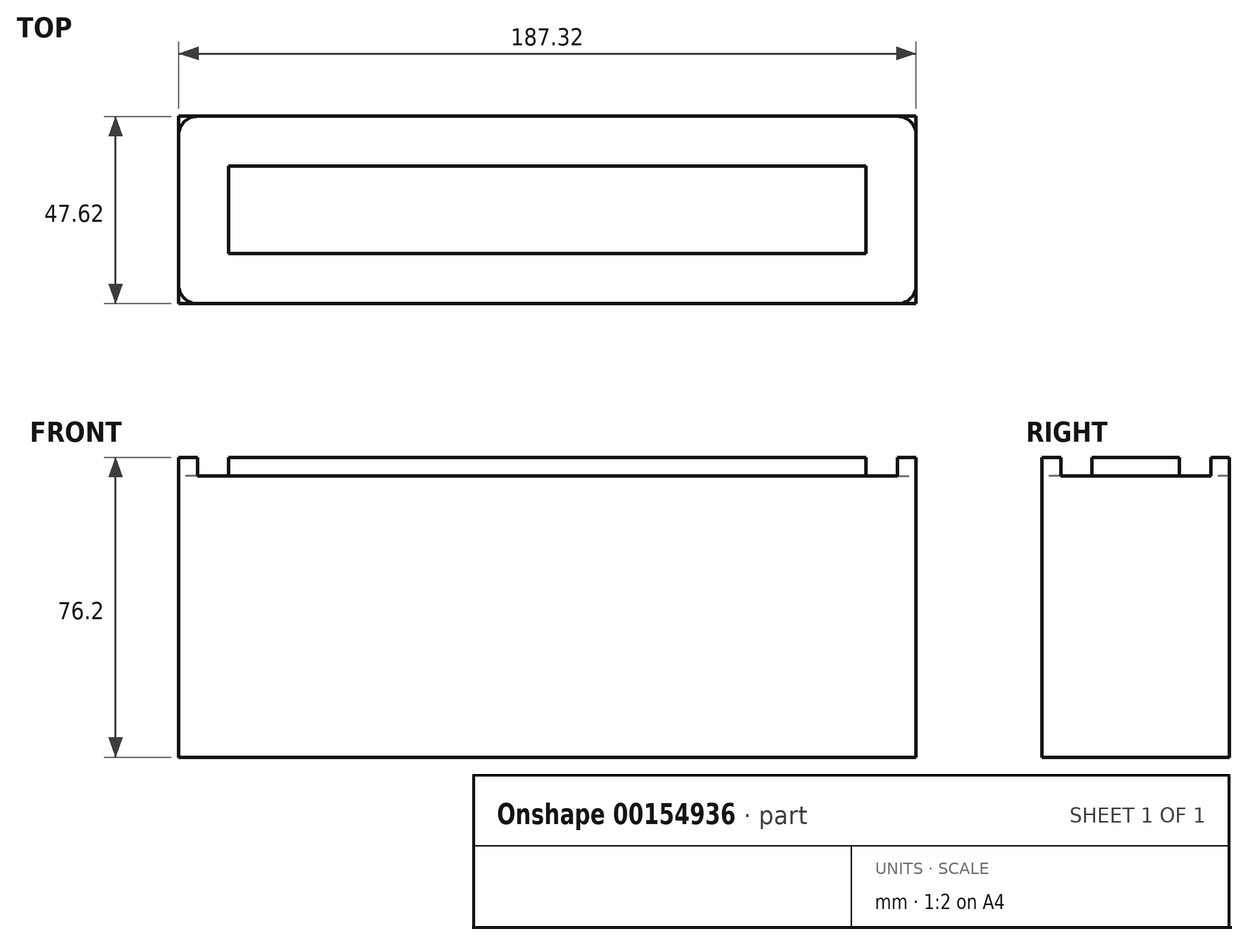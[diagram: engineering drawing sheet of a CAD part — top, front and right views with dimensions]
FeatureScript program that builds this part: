
annotation { "Feature Type Name" : "Feature", "Feature Type Description" : "" }
export const myFeature = defineFeature(function(context is Context, id is Id, definition is map)
    precondition{}
    {
        {
            var Q0;
            Q0=qCreatedBy(makeId("Top.planeOp"),FACE);
            var sketch = newSketch(context, id + "F0", { "sketchPlane" : qUnion([Q0])});
            skLineSegment(sketch, "E0.bottom", {"start": v(4.76, 0) * mm, "end": v(182.56, 0) * mm});
            skLineSegment(sketch, "E0.top", {"start": v(4.76, 47.63) * mm, "end": v(182.56, 47.63) * mm});
            skLineSegment(sketch, "E0.left", {"start": v(0, 4.76) * mm, "end": v(0, 42.86) * mm});
            skLineSegment(sketch, "E0.right", {"start": v(187.33, 4.76) * mm, "end": v(187.33, 42.86) * mm});
            skPoint(sketch, "E1.visualSharp", {"position": v(0, 47.63) * mm});
            skPoint(sketch, "E2.visualSharp", {"position": v(0, 0) * mm});
            skPoint(sketch, "E3.visualSharp", {"position": v(187.33, 0) * mm});
            skPoint(sketch, "E4.visualSharp", {"position": v(187.33, 47.62) * mm});
            skLineSegment(sketch, "E5", {"start": v(182.56, 47.63) * mm, "end": v(187.33, 47.63) * mm});
            skLineSegment(sketch, "E6", {"start": v(187.33, 42.86) * mm, "end": v(187.33, 47.62) * mm});
            skLineSegment(sketch, "E7", {"start": v(187.33, 4.76) * mm, "end": v(187.33, 0) * mm});
            skLineSegment(sketch, "E8", {"start": v(182.56, 0) * mm, "end": v(187.33, 0) * mm});
            skLineSegment(sketch, "E9", {"start": v(0, 4.76) * mm, "end": v(0, 0) * mm});
            skLineSegment(sketch, "E10", {"start": v(0, 0) * mm, "end": v(4.76, 0) * mm});
            skLineSegment(sketch, "E11", {"start": v(0, 42.86) * mm, "end": v(0, 47.63) * mm});
            skLineSegment(sketch, "E12", {"start": v(4.76, 47.63) * mm, "end": v(0, 47.63) * mm});
            skSolve(sketch);
        }
        {
            var Q0;
            Q0=makeQuery(id+"F0.imprint","IMPRINT",FACE,{"disambiguationData":[TD([[makeQuery(id+"F0.imprint","IMPRINT",EDGE,{"derivedFrom":sQuery(id+"F0.wireOp",EDGE,"E0.bottom")}),1.0]])]});
            extrude(context, id + "F1", {"entities" : qUnion([Q0]), "oppositeDirection" : true, "depth" : 76.2 * mm});
        }
        {
            var Q0;
            Q0=makeQuery(id+"F1.opExtrude","CAP_FACE",FACE,{"disambiguationData":[OSD([sQuery(id+"F0.wireOp",EDGE,"E0.bottom"),sQuery(id+"F0.wireOp",EDGE,"E0.top"),sQuery(id+"F0.wireOp",EDGE,"E0.left"),sQuery(id+"F0.wireOp",EDGE,"E0.right")])],"isStart":true});
            var sketch = newSketch(context, id + "F2", { "sketchPlane" : qUnion([Q0])});
            skLineSegment(sketch, "E13.bottom", {"start": v(12.7, 34.93) * mm, "end": v(174.63, 34.93) * mm});
            skLineSegment(sketch, "E13.top", {"start": v(12.7, 12.7) * mm, "end": v(174.63, 12.7) * mm});
            skLineSegment(sketch, "E13.left", {"start": v(12.7, 34.93) * mm, "end": v(12.7, 12.7) * mm});
            skLineSegment(sketch, "E13.right", {"start": v(174.63, 34.93) * mm, "end": v(174.63, 12.7) * mm});
            skLineSegment(sketch, "E14", {"start": v(187.33, 42.86) * mm, "end": v(187.33, 4.76) * mm});
            skLineSegment(sketch, "E15", {"start": v(0, 42.86) * mm, "end": v(0, 4.76) * mm});
            skLineSegment(sketch, "E16", {"start": v(4.76, 47.63) * mm, "end": v(182.56, 47.63) * mm});
            skLineSegment(sketch, "E17", {"start": v(182.56, 0) * mm, "end": v(4.76, 0) * mm});
            skPoint(sketch, "E18.visualSharp", {"position": v(0, 47.63) * mm});
            skArc(sketch, "E18.filletArc", {"start": v(4.76, 47.63) * mm, "mid": v(1.4, 46.23) * mm, "end": v(0, 42.86) * mm});
            skPoint(sketch, "E19.visualSharp", {"position": v(0, 0) * mm});
            skArc(sketch, "E19.filletArc", {"start": v(0, 4.76) * mm, "mid": v(1.4, 1.4) * mm, "end": v(4.76, 0) * mm});
            skPoint(sketch, "E20.visualSharp", {"position": v(187.33, 0) * mm});
            skArc(sketch, "E20.filletArc", {"start": v(182.56, 0) * mm, "mid": v(185.93, 1.4) * mm, "end": v(187.33, 4.76) * mm});
            skPoint(sketch, "E21.visualSharp", {"position": v(187.33, 47.63) * mm});
            skArc(sketch, "E21.filletArc", {"start": v(187.33, 42.86) * mm, "mid": v(185.93, 46.23) * mm, "end": v(182.56, 47.63) * mm});
            skSolve(sketch);
        }
        {
            var Q0;
            Q0 = qSketchRegion(id + "F2", true);
            extrude(context, id + "F3", {"entities" : qUnion([Q0]), "operationType" : NewBodyOperationType.REMOVE, "oppositeDirection" : true, "depth" : 4.76 * mm});
        }
    });
